# Revit family: 1295 Pon Coffee Table D90
name_source: partatom
category: Furniture
revit_build: Autodesk Revit 2017 (Build: 20171027_0315(x64)
units: mm (PartAtom-declared; Revit-internal decimal feet)

## family parameters
Always vertical = Yes
Cut with Voids When Loaded = No
OmniClass Number = 23.40.20.00
OmniClass Title = General Furniture and Specialties
Room Calculation Point = No
Shared = No
Work Plane-Based = No

## types (1)
- 1295 Pon Coffee Table D90
    Description = Pon is a series of solid wood side tables in different sizes that are both very stable, versatile and which can be used as either stand-alone furniture or combined in different heights. The smaller Pon tables are modest in size, but large enough for a book, a glass or a tray.
    Design year = 2015
    Diameter = 90 cm
    Frame Horizontal = FF Oak Black Lacquered horizontal
    Frame Vertical = FF Oak Black Lacquered vertical
    Height = 38 cm
    Item No. = 1295
    Manufacturer = Fredericia Furniture
    Model = Pon Coffee Table D90
    URL = https://www.fredericia.com
    Variation Frame - Extra charge = Available in other kinds of wood
    Variation Frame - Standard = Available in other kinds of wood
    Weight = 28,5 kg

## geometry (parser evidence)
native form markers: Sweep x3
no freeform markers — native parametric forms only
